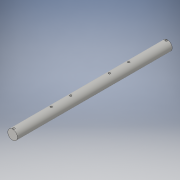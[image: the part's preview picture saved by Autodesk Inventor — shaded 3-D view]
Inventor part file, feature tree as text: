
AUTODESK INVENTOR PART (.ipt)
format: ipt  version: 2016 (Build 200138000, 138)  size: 127,488 bytes
history: native  units: in
note: dims shown in document units (in); Inventor stores cm internally (conversion verified against a paired STEP export)
features: extrude x3, sketch x3
ambient origin geometry x8: Origin, YZ Plane, XZ Plane, XY Plane, X Axis, Y Axis, Z Axis, Center Point
bodies: Solid1 (feature_tree)
feature tree (6):
  extrude  "Extrusion1"  Depth=8.0in TaperAngle=0.0deg
  extrude  "Extrusion4"  Depth=0.06in
  extrude  "Extrusion10"  Depth=2.0in TaperAngle=0.0deg
  sketch  "Sketch1"  dims[d0=0.5in d1=8.0in d2=0.0in]
  sketch  "Sketch4"  dims[d13=0.06in d15=0.06in]
  sketch  "Sketch8"  dims[d16=0.1in d17=0.6in d18=0.0in d19=0.1in d50=2.0in d51=0.1in d58=1.0in d59=0.1in d60=2.0in d61=0.1in d62=1.0in d63=0.1in d64=1.0in d65=0.0in]
